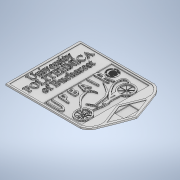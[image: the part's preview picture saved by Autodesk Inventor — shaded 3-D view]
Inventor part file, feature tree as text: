
AUTODESK INVENTOR PART (.ipt)
format: ipt  version: 2020 (Build 240168000, 168)  size: 27,844,608 bytes
history: native  units: mm
features: move_body x17, extrude x12, sketch x9, plane x7, other x7, direct_edit x1
ambient origin geometry x8: Origin, YZ Plane, XZ Plane, XY Plane, X Axis, Y Axis, Z Axis, Center Point
bodies: Solid1 (feature_tree), Solid2 (feature_tree), Solid3 (feature_tree), Solid4 (feature_tree)
feature tree (53):
  sketch  "Sketch1"  dims[d45=20.0mm d46=0.0mm d48=14.0mm d49=0.0mm]
  extrude  "Extrusion1"  Depth=14.0mm TaperAngle=0.0deg
  extrude  "Extrusion2"  Depth=3.0mm TaperAngle=0.0deg
  extrude  "Extrusion3"  Depth=2.0mm TaperAngle=0.0deg
  extrude  "Extrusion4"  Depth=2.0mm TaperAngle=0.0deg
  plane  "Work Plane1"
  extrude  "Extrusion5"  Depth=2.0mm TaperAngle=0.0deg
  plane  "Work Plane2"
  sketch  "Sketch3"  dims[d62=2.0mm d63=0.0mm d64=2.0mm d65=0.0mm]
  plane  "Work Plane3"
  sketch  "Sketch4"  dims[d66=2.0mm d67=0.0mm d68=2.0mm d69=0.0mm]
  plane  "Work Plane4"
  sketch  "Sketch5"  dims[d70=2.0mm d71=0.0mm d72=2.0mm d73=0.0mm]
  plane  "Work Plane5"
  sketch  "Sketch6"  dims[d74=2.0mm d75=0.0mm d76=20.0mm d77=10.0mm d78=10.0mm]
  plane  "Work Plane6"
  sketch  "Sketch7"  dims[d79=30.0mm d80=10.0mm d81=10.0mm d82=-1710.0mm d83=-76.0mm d84=0.0mm]
  plane  "Work Plane7"
  sketch  "Sketch8"  dims[d85=-33.0mm d86=0.0mm d87=200.0mm d89=90.0deg]
  extrude  "Extrusion6"  Depth=10.0mm
  extrude  "Extrusion7"  TaperAngle=0.0deg  [1 undecoded]
  extrude  "Extrusion8"  TaperAngle=90.0deg  [1 undecoded]
  extrude  "Extrusion9"  [1 undecoded]
  extrude  "Extrusion10"  TaperAngle=0.0deg  [1 undecoded]
  extrude  "Extrusion11"  TaperAngle=180.0deg  [1 undecoded]
  direct_edit  "Direct Edit1"
  move_body  "Move Body5"
  move_body  "Move Body6"
  other  "Logo_UPB"
  other  "MeshFeature2"
  move_body  "Move Body7"
  move_body  "Move Body8"
  move_body  "Move Body9"
  move_body  "Move Body10"
  move_body  "Move Body11"
  move_body  "Move Body12"
  move_body  "Move Body13"
  move_body  "Move Body14"
  move_body  "Move Body15"
  move_body  "Move Body16"
  extrude  "Extrusion12"  Depth=3.0mm TaperAngle=0.0deg
  other  "IMST_lowpoly_3D"
  other  "MeshFeature3"
  move_body  "Move Body17"
  move_body  "Move Body18"
  move_body  "Move Body19"
  move_body  "Move Body20"
  move_body  "Move Body21"
  other  "Image1"
  sketch  "Sketch2"  dims[d50=10.0mm d51=0.0mm d52=3.0mm d53=0.0mm]
  sketch  "Sketch9"  dims[d90=0.0mm d91=3.0mm d92=0.0mm d93=-15.707963mm d94=0.0mm d95=0.0mm d96=-250.0mm d97=180.0deg d98=0.0mm d99=3.0mm d100=0.0mm d101=0.0mm d102=2.0mm d103=0.0mm d104=0.0mm d105=0.0mm d106=-500.0mm d107=0.0mm d108=1.0mm d109=0.0mm d110=10.0mm d111=0.0mm d112=0.0mm d113=80.0mm d115=360.0deg d118=80.0mm d119=360.0deg d120=3.0mm d121=0.0mm d122=90.0deg d123=90.0deg d124=180.0deg d125=200.0mm d126=0.0mm d127=205.0mm d128=2.0mm d129=2.0mm d130=0.0mm d47=0.5mm]
  other  "Scale1"
  other  "Scale2"
note: 5 required parameter values undecoded (feature->parameter linkage not recoverable at this tier; creation-order binding heuristic only, values carry confidence <= 0.55)
